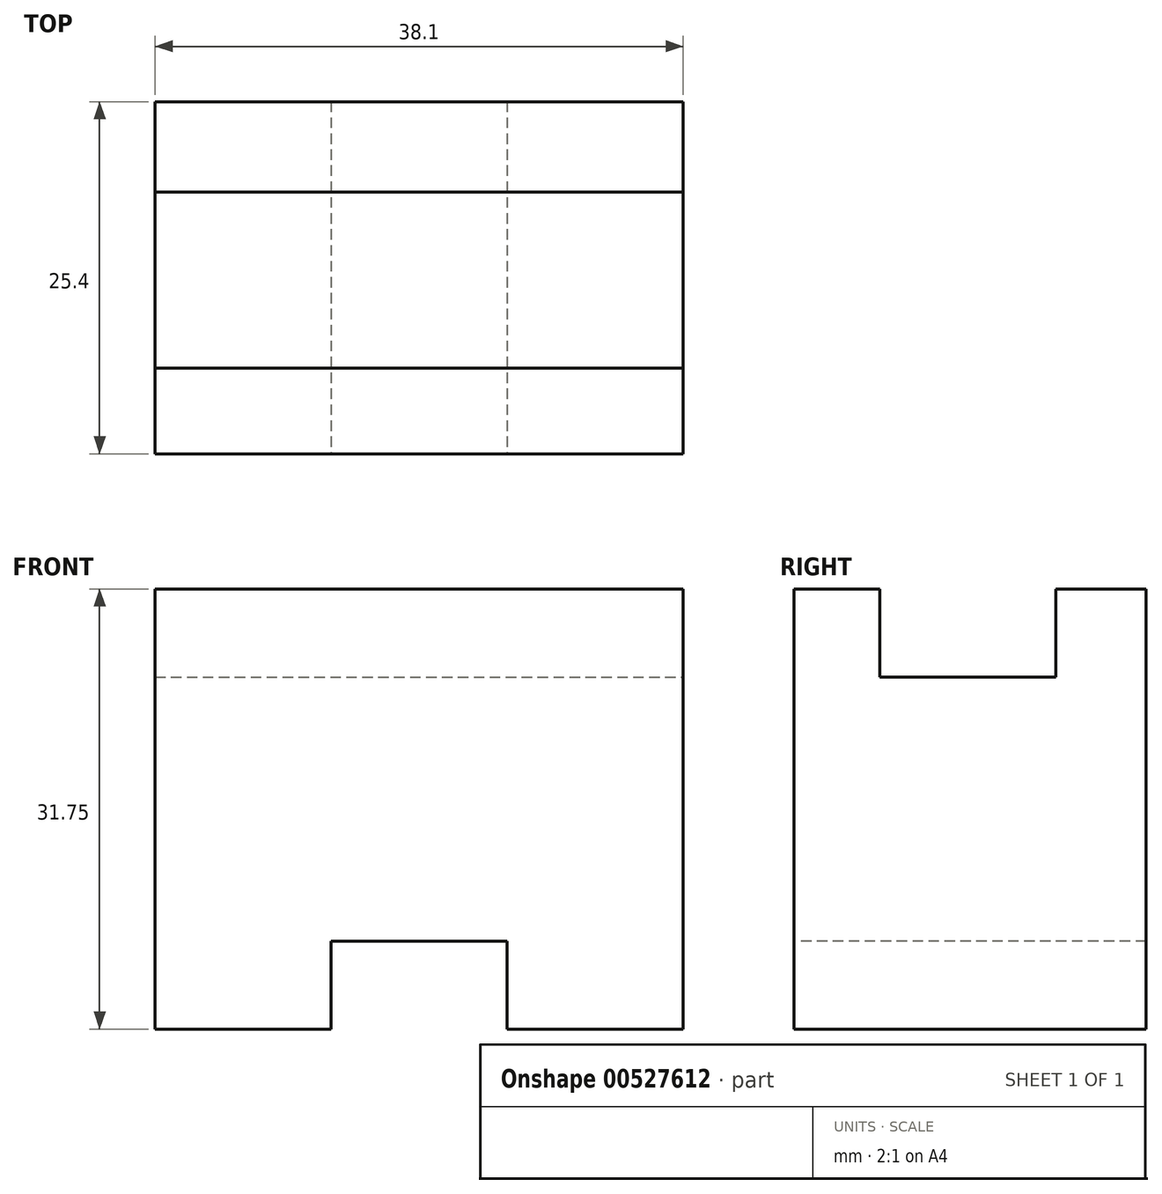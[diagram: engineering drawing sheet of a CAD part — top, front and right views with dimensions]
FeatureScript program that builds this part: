
annotation { "Feature Type Name" : "Feature", "Feature Type Description" : "" }
export const myFeature = defineFeature(function(context is Context, id is Id, definition is map)
    precondition{}
    {
        {
            var Q0;
            Q0=qCreatedBy(makeId("Front.planeOp"),FACE);
            var sketch = newSketch(context, id + "F0", { "sketchPlane" : qUnion([Q0])});
            skLineSegment(sketch, "E0.bottom", {"start": v(-23.27, 0) * mm, "end": v(14.83, 0) * mm});
            skLineSegment(sketch, "E0.top", {"start": v(-23.27, 31.75) * mm, "end": v(14.83, 31.75) * mm});
            skLineSegment(sketch, "E0.left", {"start": v(-23.27, 0) * mm, "end": v(-23.27, 31.75) * mm});
            skLineSegment(sketch, "E0.right", {"start": v(14.83, 0) * mm, "end": v(14.83, 31.75) * mm});
            skSolve(sketch);
        }
        {
            var Q0;
            Q0 = qSketchRegion(id + "F0", true);
            extrude(context, id + "F1", {"entities" : qUnion([Q0]), "oppositeDirection" : true, "depth" : 25.4 * mm, "offsetDistance" : 25.4 * mm});
        }
        {
            var Q0;
            Q0=makeQuery(id+"F1.opExtrude","SWEPT_FACE",FACE,{"disambiguationData":[OSD([sQuery(id+"F0.wireOp",EDGE,"E0.top")])]});
            var sketch = newSketch(context, id + "F2", { "sketchPlane" : qUnion([Q0])});
            skLineSegment(sketch, "E1.bottom", {"start": v(-23.27, 6.2) * mm, "end": v(14.83, 6.2) * mm});
            skLineSegment(sketch, "E1.top", {"start": v(-23.27, 18.88) * mm, "end": v(14.83, 18.88) * mm});
            skLineSegment(sketch, "E1.left", {"start": v(-23.27, 6.2) * mm, "end": v(-23.27, 18.88) * mm});
            skLineSegment(sketch, "E1.right", {"start": v(14.83, 6.2) * mm, "end": v(14.83, 18.88) * mm});
            skSolve(sketch);
        }
        {
            var Q0;
            Q0=makeQuery(id+"F2.imprint","IMPRINT",FACE,{"disambiguationData":[TD([[makeQuery(id+"F2.imprint","IMPRINT",EDGE,{"derivedFrom":sQuery(id+"F2.wireOp",EDGE,"E1.bottom")}),1.0]])]});
            extrude(context, id + "F3", {"entities" : qUnion([Q0]), "operationType" : NewBodyOperationType.REMOVE, "oppositeDirection" : true, "depth" : 6.35 * mm, "offsetDistance" : 25.4 * mm});
        }
        {
            var Q0;
            Q0=makeQuery(id+"F1.opExtrude","CAP_FACE",FACE,{"disambiguationData":[OSD([sQuery(id+"F0.wireOp",EDGE,"E0.bottom"),sQuery(id+"F0.wireOp",EDGE,"E0.top"),sQuery(id+"F0.wireOp",EDGE,"E0.left"),sQuery(id+"F0.wireOp",EDGE,"E0.right")])],"isStart":true});
            var sketch = newSketch(context, id + "F4", { "sketchPlane" : qUnion([Q0])});
            skLineSegment(sketch, "E2", {"start": v(-23.27, 0) * mm, "end": v(-10.57, 0) * mm});
            skLineSegment(sketch, "E3", {"start": v(-10.57, 0) * mm, "end": v(-10.57, 6.35) * mm});
            skLineSegment(sketch, "E4", {"start": v(-10.57, 6.35) * mm, "end": v(2.13, 6.35) * mm});
            skLineSegment(sketch, "E5", {"start": v(2.13, 6.35) * mm, "end": v(2.13, 0) * mm});
            skLineSegment(sketch, "E6", {"start": v(2.13, 0) * mm, "end": v(14.83, 0) * mm});
            skSolve(sketch);
        }
        {
            var Q0;
            {var subQ0=sQuery(id+"F4.wireOp",EDGE,"E3");Q0=makeQuery(id+"F4.imprint","IMPRINT",FACE,{"disambiguationData":[TD([[makeQuery(id+"F4.imprint","IMPRINT",EDGE,{"derivedFrom":subQ0}),-1.0]])]});}
            extrude(context, id + "F5", {"entities" : qUnion([Q0]), "operationType" : NewBodyOperationType.REMOVE, "oppositeDirection" : true, "depth" : 25.4 * mm, "offsetDistance" : 25.4 * mm});
        }
    });
